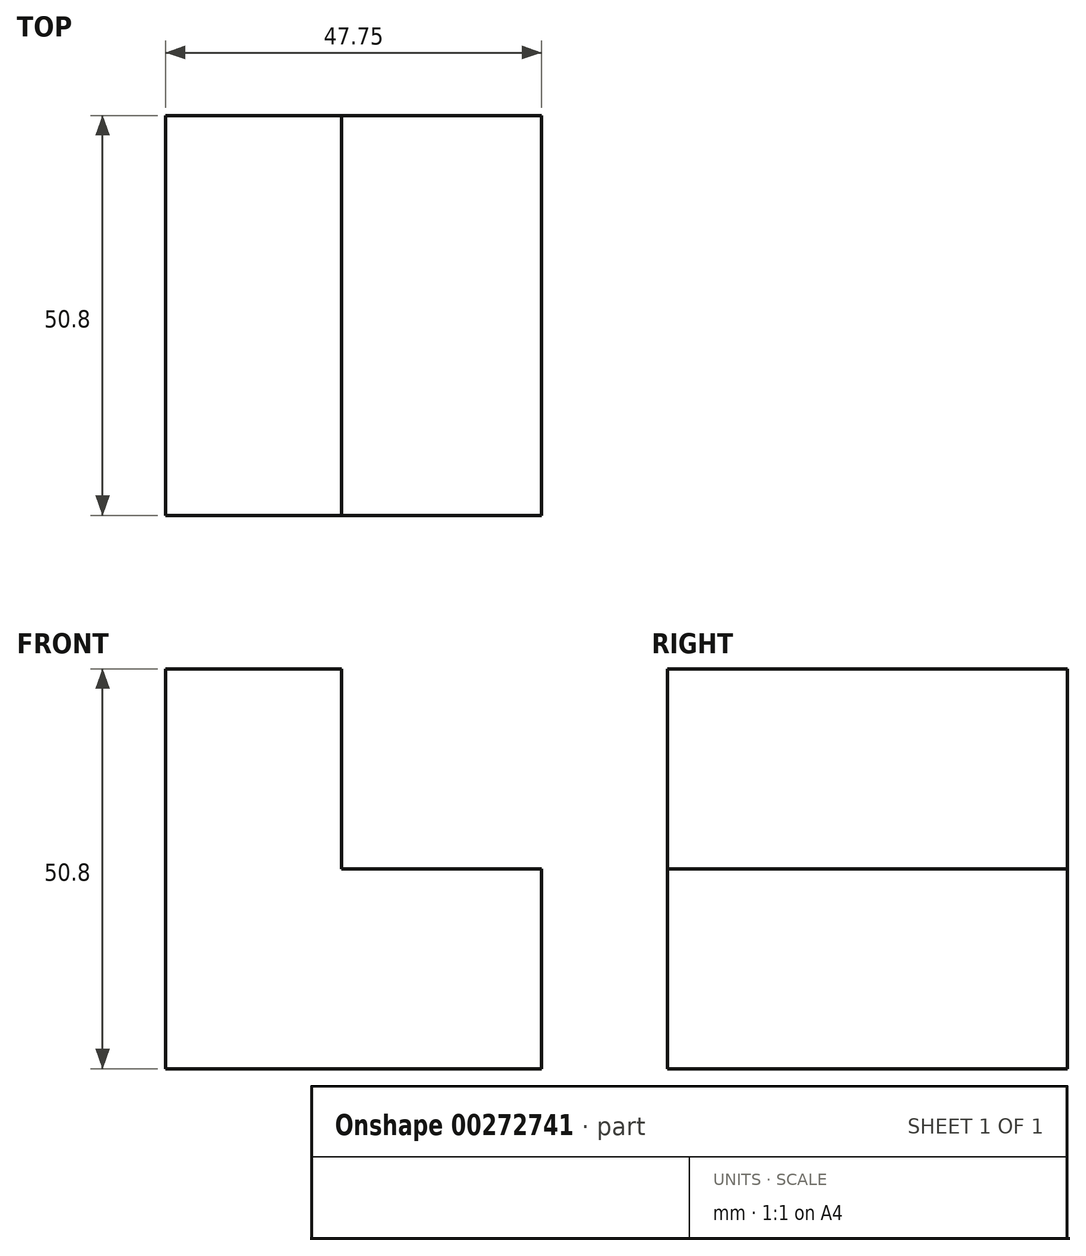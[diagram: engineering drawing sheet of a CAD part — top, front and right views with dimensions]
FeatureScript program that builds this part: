
annotation { "Feature Type Name" : "Feature", "Feature Type Description" : "" }
export const myFeature = defineFeature(function(context is Context, id is Id, definition is map)
    precondition{}
    {
        {
            var Q0;
            Q0=qCreatedBy(makeId("Front.planeOp"),FACE);
            var sketch = newSketch(context, id + "F0", { "sketchPlane" : qUnion([Q0])});
            skLineSegment(sketch, "E0", {"start": v(0, 0) * mm, "end": v(-50.8, 0) * mm});
            skLineSegment(sketch, "E1", {"start": v(-50.8, 0) * mm, "end": v(-50.8, 50.8) * mm});
            skLineSegment(sketch, "E2", {"start": v(-50.8, 50.8) * mm, "end": v(-28.45, 50.8) * mm});
            skLineSegment(sketch, "E3", {"start": v(-28.45, 50.8) * mm, "end": v(-28.45, 25.4) * mm});
            skLineSegment(sketch, "E4", {"start": v(-28.45, 25.4) * mm, "end": v(-3.05, 25.4) * mm});
            skLineSegment(sketch, "E5", {"start": v(-3.05, 25.4) * mm, "end": v(-3.05, 0) * mm});
            skSolve(sketch);
        }
        {
            var Q0;
            {var subQ0=sQuery(id+"F0.wireOp",EDGE,"E1");Q0=makeQuery(id+"F0.imprint","IMPRINT",FACE,{"disambiguationData":[TD([[makeQuery(id+"F0.imprint","IMPRINT",EDGE,{"derivedFrom":subQ0}),-1.0]])]});}
            extrude(context, id + "F1", {"entities" : qUnion([Q0]), "depth" : 50.8 * mm});
        }
    });
